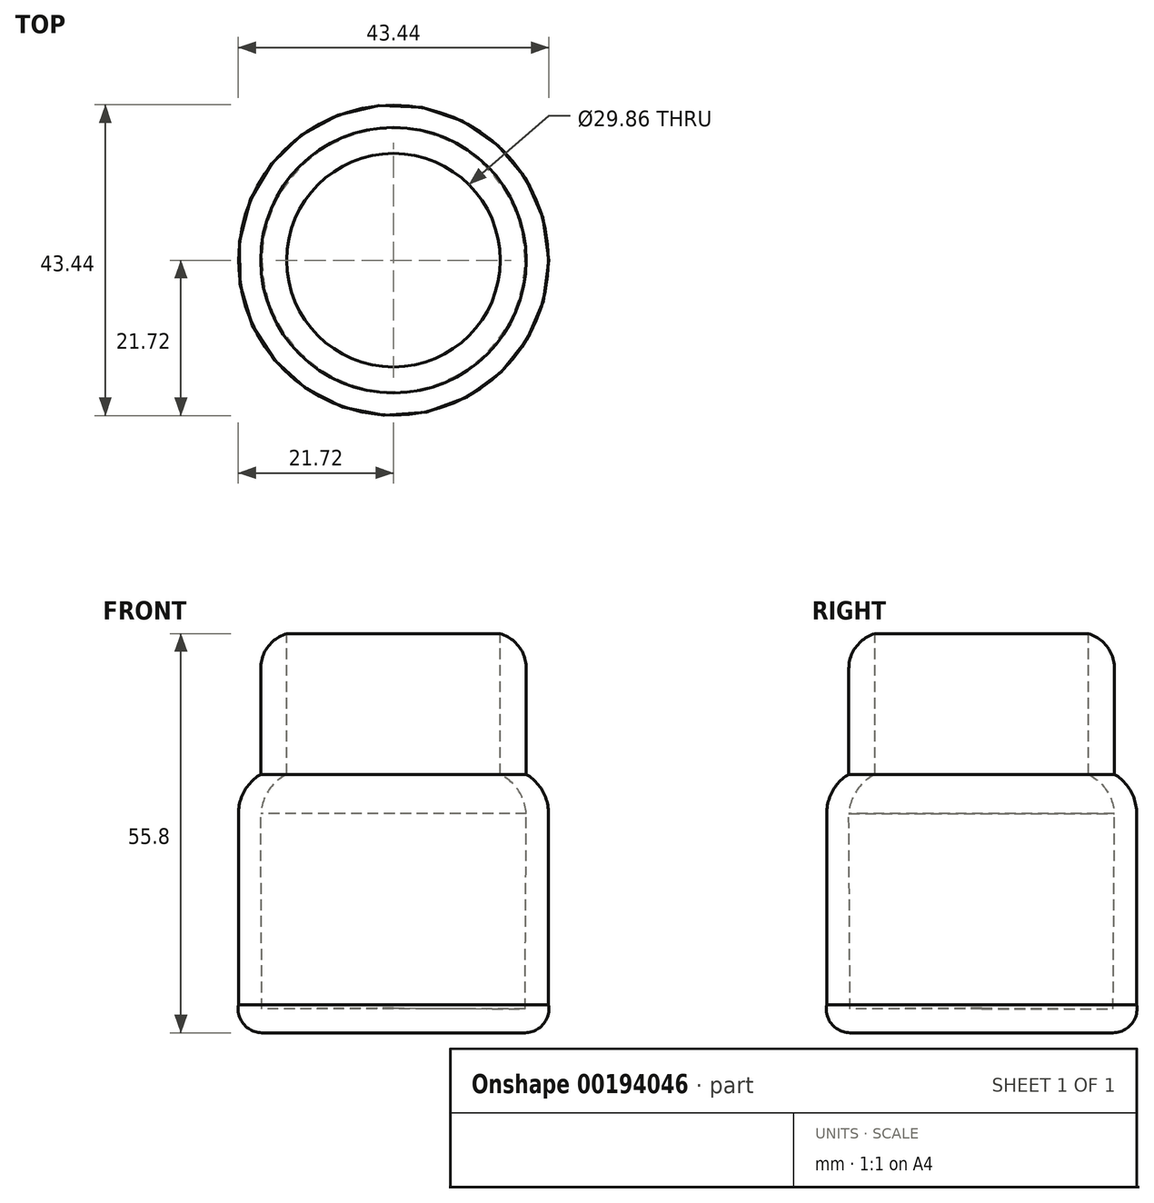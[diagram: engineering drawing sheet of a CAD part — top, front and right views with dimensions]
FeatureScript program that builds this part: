
annotation { "Feature Type Name" : "Feature", "Feature Type Description" : "" }
export const myFeature = defineFeature(function(context is Context, id is Id, definition is map)
    precondition{}
    {
        {
            var Q0;
            Q0=qCreatedBy(makeId("Front.planeOp"),FACE);
            var sketch = newSketch(context, id + "F0", { "sketchPlane" : qUnion([Q0])});
            skLineSegment(sketch, "E0", {"start": v(0, 0) * mm, "end": v(18.39, 0) * mm});
            skArc(sketch, "E1", {"start": v(18.39, 0) * mm, "mid": v(20.94, 1.2) * mm, "end": v(21.66, 3.91) * mm});
            skLineSegment(sketch, "E2", {"start": v(21.66, 3.91) * mm, "end": v(21.66, 30.68) * mm});
            skArc(sketch, "E3", {"start": v(21.66, 30.68) * mm, "mid": v(20.84, 33.81) * mm, "end": v(18.57, 36.14) * mm});
            skLineSegment(sketch, "E4", {"start": v(18.57, 36.14) * mm, "end": v(18.57, 55.8) * mm});
            skLineSegment(sketch, "E5", {"start": v(18.57, 55.8) * mm, "end": v(14.93, 55.8) * mm});
            skLineSegment(sketch, "E6", {"start": v(14.93, 55.8) * mm, "end": v(14.93, 36.14) * mm});
            skArc(sketch, "E7", {"start": v(18.57, 30.68) * mm, "mid": v(17.46, 33.88) * mm, "end": v(14.93, 36.14) * mm});
            skLineSegment(sketch, "E8", {"start": v(18.57, 30.68) * mm, "end": v(18.39, 3.33) * mm});
            skLineSegment(sketch, "E9", {"start": v(18.39, 3.33) * mm, "end": v(0, 3.45) * mm});
            skLineSegment(sketch, "E10", {"start": v(0, 3.45) * mm, "end": v(0, 0) * mm});
            skSolve(sketch);
        }
        {
            var Q0;
            Q0=makeQuery(id+"F0.imprint","IMPRINT",FACE,{"disambiguationData":[TD([[makeQuery(id+"F0.imprint","IMPRINT",EDGE,{"derivedFrom":sQuery(id+"F0.wireOp",EDGE,"E0")}),1.0]])]});
            var Q1;
            Q1=sQuery(id+"F0.wireOp",EDGE,"E10");
            revolve(context, id + "F1", {"entities" : qUnion([Q0]), "axis" : qUnion([Q1]), "revolveType" : RevolveType.FULL});
        }
        {
            var Q0;
            Q0=makeQuery(id+"F1.opRevolve","SWEPT_EDGE",EDGE,{"disambiguationData":[OSD([sQuery(id+"F0.wireOp",EDGE,"E4"),sQuery(id+"F0.wireOp",EDGE,"E5")])]});
            fillet(context, id + "F2", {"entities" : qUnion([Q0]), "radius" : 5.08 * mm, "tangentPropagation" : true, "allowEdgeOverflow" : false});
        }
    });
